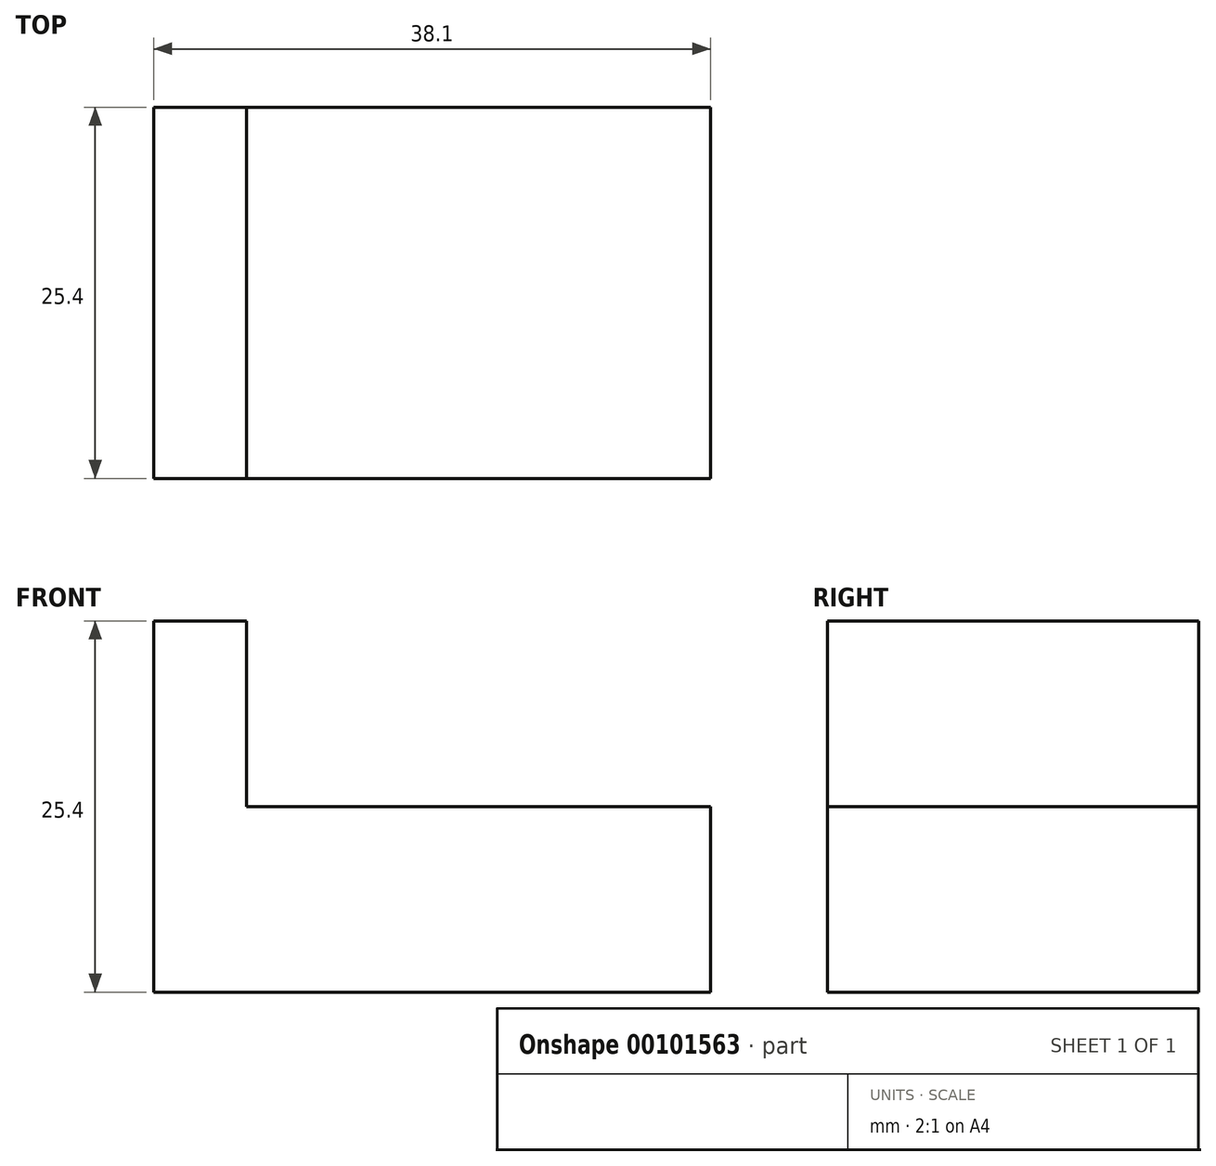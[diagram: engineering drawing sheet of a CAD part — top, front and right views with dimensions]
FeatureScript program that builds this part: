
annotation { "Feature Type Name" : "Feature", "Feature Type Description" : "" }
export const myFeature = defineFeature(function(context is Context, id is Id, definition is map)
    precondition{}
    {
        {
            var Q0;
            Q0=qCreatedBy(makeId("Front.planeOp"),FACE);
            var sketch = newSketch(context, id + "F0", { "sketchPlane" : qUnion([Q0])});
            skLineSegment(sketch, "E0", {"start": v(0, 0) * mm, "end": v(38.1, 0) * mm});
            skLineSegment(sketch, "E1", {"start": v(38.1, 0) * mm, "end": v(38.1, 12.7) * mm});
            skLineSegment(sketch, "E2", {"start": v(38.1, 12.7) * mm, "end": v(6.35, 12.7) * mm});
            skLineSegment(sketch, "E3", {"start": v(6.35, 12.7) * mm, "end": v(6.35, 25.4) * mm});
            skLineSegment(sketch, "E4", {"start": v(6.35, 25.4) * mm, "end": v(0, 25.4) * mm});
            skLineSegment(sketch, "E5", {"start": v(0, 25.4) * mm, "end": v(0, 0) * mm});
            skSolve(sketch);
        }
        {
            var Q0;
            Q0 = qSketchRegion(id + "F0", true);
            extrude(context, id + "F1", {"entities" : qUnion([Q0]), "oppositeDirection" : true, "depth" : 25.4 * mm});
        }
    });
